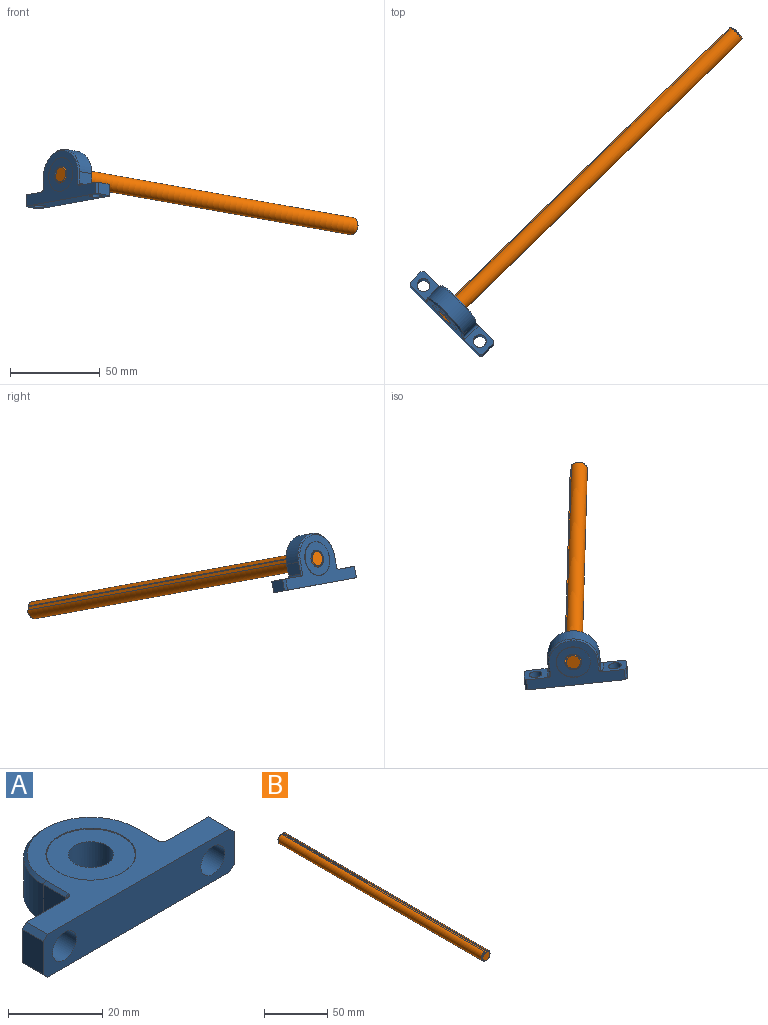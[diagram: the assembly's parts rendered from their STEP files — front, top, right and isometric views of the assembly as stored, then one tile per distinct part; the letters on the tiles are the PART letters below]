
ASSEMBLY  parts=2 mates=1
PART A: 36 faces, bbox 57.2x28.6x12.9 mm
  f0: cylinder r=3.57mm len=7.14mm, axis (0,1,0), area 142.5mm2, adj f11,f13
  f1: cylinder r=3.57mm len=7.14mm, axis (0,1,0), area 142.5mm2, adj f9,f11
  f2: cylinder r=4.76mm len=10.99mm, axis (0,0,1), area 328.7mm2, adj f33,f35
  f3: cone r=9.53mm half-angle=45deg, axis (0,0,-1), area 10.7mm2, adj f6,f35
  f4: cylinder r=9.4mm len=18.8mm, axis (0,0,1), area 573.7mm2, adj f33,f34
  f5: cylinder r=9.53mm len=19.05mm, axis (0,0,1), area 581.4mm2, adj f16,f34
  f6: cylinder r=9.53mm len=19.05mm, axis (0,0,1), area 15.2mm2, adj f3,f15
  f7: cylinder r=14.29mm len=28.58mm, axis (0,0,-1), area 430.4mm2, adj f8,f14,f18,f21
  f8: plane 9.59x6.67mm, normal (-1,0,0), area 63.9mm2, adj f7,f19,f22,f24
  f9: plane 13.25x11.11mm, normal (0,1,0), area 103mm2, adj f1,f10,f15,f16,f23,f24,f25,f29
  f10: plane 8.57x6.35mm, normal (-1,0,0), area 54.4mm2, adj f9,f11,f29,f30
  f11: plane 57.15x11.11mm, normal (0,-1,0), area 551.7mm2, adj f0,f1,f10,f12,f15,f16,f29,f30
  f12: plane 8.57x6.35mm, normal (1,0,0), area 54.4mm2, adj f11,f13,f31,f32
  f13: plane 13.25x11.11mm, normal (0,1,0), area 103mm2, adj f0,f12,f15,f16,f26,f27,f28,f31
  f14: plane 9.59x6.67mm, normal (1,0,0), area 63.9mm2, adj f7,f17,f20,f27
  f15: plane 54.61x27.81mm, normal (0,0,1), area 564.8mm2, adj f6,f9,f11,f13,f20,f21,f22,f23
  f16: plane 54.61x27.81mm, normal (0,0,-1), area 564.8mm2, adj f5,f9,f11,f13,f17,f18,f19,f25
  f17: plane 6.67x0.76mm, normal (0.71,0,-0.71), area 7.2mm2, adj f14,f16,f18,f28
  f18: cone r=14.29mm half-angle=45deg, axis (0,0,1), area 47.1mm2, adj f7,f16,f17,f19
  f19: plane 6.67x0.76mm, normal (-0.71,0,-0.71), area 7.2mm2, adj f8,f16,f18,f25
  f20: plane 6.67x0.76mm, normal (0.71,0,0.71), area 7.2mm2, adj f14,f15,f21,f26
  f21: cone r=13.53mm half-angle=45deg, axis (0,0,-1), area 47.1mm2, adj f7,f15,f20,f22
  f22: plane 6.67x0.76mm, normal (-0.71,0,0.71), area 7.2mm2, adj f8,f15,f21,f23
  f23: cylinder r=1.27mm len=2.03mm, axis (-0.71,0,-0.71), area 1.6mm2, adj f9,f15,f22,f24
  f24: cylinder r=1.27mm len=10.64mm, axis (0,0,1), area 19.9mm2, adj f8,f9,f23,f25
  f25: cylinder r=1.27mm len=2.03mm, axis (-0.71,0,0.71), area 1.6mm2, adj f9,f16,f19,f24
  f26: cylinder r=1.27mm len=2.03mm, axis (-0.71,0,0.71), area 1.6mm2, adj f13,f15,f20,f27
  f27: cylinder r=1.27mm len=10.64mm, axis (0,0,1), area 19.9mm2, adj f13,f14,f26,f28
  f28: cylinder r=1.27mm len=2.03mm, axis (-0.71,0,-0.71), area 1.6mm2, adj f13,f16,f17,f27
  f29: plane 6.35x1.27mm, normal (-0.71,0,-0.71), area 11.4mm2, adj f9,f10,f11,f16
  f30: plane 6.35x1.27mm, normal (-0.71,0,0.71), area 11.4mm2, adj f9,f10,f11,f15
  f31: plane 6.35x1.27mm, normal (0.71,0,-0.71), area 11.4mm2, adj f11,f12,f13,f16
  f32: plane 6.35x1.27mm, normal (0.71,0,0.71), area 11.4mm2, adj f11,f12,f13,f15
  f33: plane 18.8x18.8mm, normal (0,0,-1), area 206.2mm2, adj f2,f4
  f34: plane 19.05x19.05mm, normal (0,0,-1), area 7.5mm2, adj f4,f5
  f35: plane 18.8x18.8mm, normal (0,0,1), area 206.2mm2, adj f2,f3
PART B: 8 faces, bbox 9.5x228.6x9.4 mm
  f0: cone r=4.05mm half-angle=45deg, axis (0,1,0), area 25.5mm2, adj f2,f3,f5,f6
  f1: cone r=4.76mm half-angle=45deg, axis (0,-1,0), area 25.5mm2, adj f2,f4,f5,f6
  f2: cylinder r=4.76mm len=227.17mm, axis (0,1,0), area 6251mm2, adj f0,f1,f5,f6
  f3: plane 8.1x7.92mm, normal (0,-1,0), area 50.5mm2, adj f0,f5,f6,f7
  f4: plane 8.1x7.92mm, normal (0,1,0), area 50.5mm2, adj f1,f5,f6,f7
  f5: plane 228.62x1.06mm, normal (1,0,0), area 237.1mm2, adj f0,f1,f2,f3,f4,f7
  f6: plane 228.62x1.06mm, normal (-1,0,0), area 237.1mm2, adj f0,f1,f2,f3,f4,f7
  f7: plane 228.6x2.38mm, normal (0,0,1), area 544.4mm2, adj f3,f4,f5,f6
PLACE A rot(axis=(0.84,-0.42,-0.35),89.8deg) t=(-15.55,-21.41,15.11)mm fixed
PLACE B rot(axis=(-0.42,-0.81,-0.41),83.1deg) t=(61.72,53.87,1.42)mm
MATE revolute B.f3 <-> A.f2  axis (-0.71,-0.69,0.13) through (-19.5,-25.26,15.81)mm
